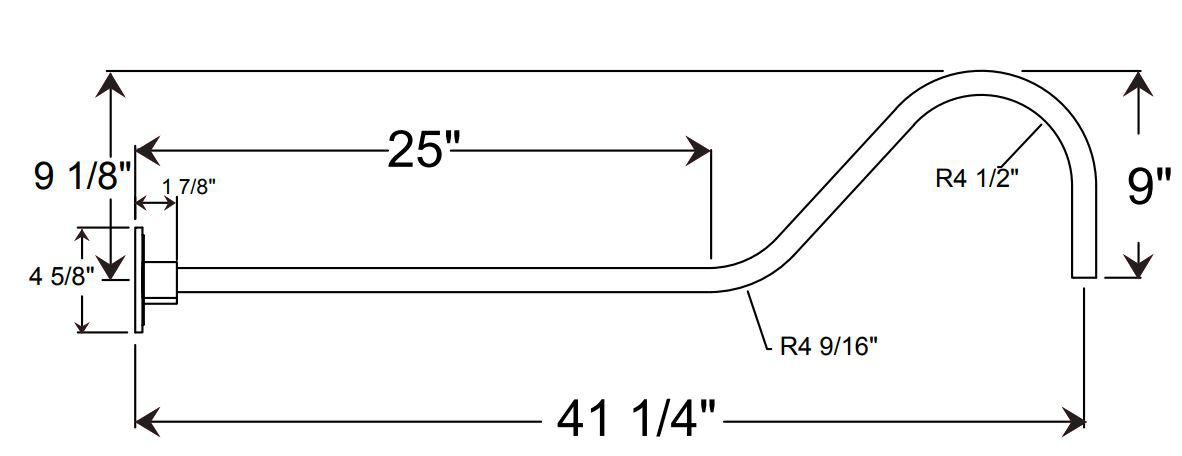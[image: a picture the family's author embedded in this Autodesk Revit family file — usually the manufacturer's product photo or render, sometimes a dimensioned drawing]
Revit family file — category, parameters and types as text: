
# Revit family: Azalea(12,16,20,24) LED
name_source: partatom
category: Lighting Fixtures
units: mm (PartAtom-declared; Revit-internal decimal feet)

## family parameters
Always vertical = Yes
Cut with Voids When Loaded = No
Light Source = Yes
OmniClass Number = 23.80.70.00
OmniClass Title = Lighting
Part Type = Normal
Room Calculation Point = No
Round Connector Dimension = Use Diameter
Shared = No
Work Plane-Based = No

## types (4) — shared parameters
Body Colour = Spun aluminium
Body Material = body
CRI = >90
Color Filter = 16777215
Construction Material = Heavy Duty spun aluminum.
Default Elevation = 0' - 0"
Description = 120-277 Voltage
Dimming = 1%
Dimming Lamp Color Temperature Shift = <None>
Efficiency = 65-125 lumens per watt
Fixture Finish = Fixture Finish
GLASS = Glass
Lamp = LED
Life = L70 50,000 hours
Load Classification = Lighting
Manufacturer = ANP Lighting
Power Factor = 1
Tilt Angle = 90.00°
URL = https://www.anplighting.com
Voltage = 277 V
Warranty = 5 year limited warranty

## per-type parameters (varying)
| type | Apparent Load | Fixture Diameter | Fixture Height | MDA12 | MDA16 | MDA20 | MDA24 | Photometric Web File | Wattage Comments | Weight |
| MDA12 | 10 VA | 1' - 0" | 0' - 9 1/2" | Yes | No | No | No | MDA12M010LD35K.IES | 10W | 4.0lbs |
| MDA16 | 16 VA | 1' - 4" | 1' - 0 1/2" | No | Yes | No | No | MDA16M016LD35K.IES | 16W | 4.5lbs |
| MDA20 | 16 VA | 1' - 8" | 1' - 4" | No | No | Yes | No | MDA20M016LD35K.IES | 16W | 5.0lbs |
| MDA24 | 16 VA | 2' - 0" | 1' - 7" | No | No | No | Yes | MDA24M024LD35K.IES | 16W | 5.5lbs |

note: column(s) folded — value = type name in every type: Model

## geometry (parser evidence)
native form markers: Sweep x44
no freeform markers — native parametric forms only
